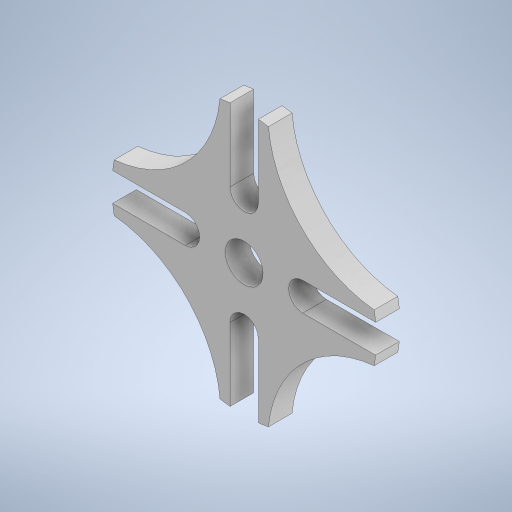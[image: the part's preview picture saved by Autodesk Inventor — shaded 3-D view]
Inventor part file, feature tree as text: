
AUTODESK INVENTOR PART (.ipt)
format: ipt  version: 2024 (Build 280153000, 153)  size: 276,480 bytes
history: native  units: mm
features: extrude x2, sketch x2, pattern_circular x1
ambient origin geometry x8: Origin, YZ Plane, XZ Plane, XY Plane, X Axis, Y Axis, Z Axis, Center Point
bodies: Solid1 (feature_tree)
feature tree (5):
  extrude  "Extrusion1"  Depth=5.0mm TaperAngle=0.0deg
  extrude  "Extrusion2"  Depth=5.0mm
  pattern_circular  "Circular Pattern1"  Count=6  [1 undecoded]
  sketch  "Sketch1"  dims[d0=56.0mm d1=5.0mm d2=0.0mm]
  sketch  "Sketch2"  dims[d3=30.0mm d4=30.0mm d5=60.0mm d6=60.0mm d7=50.0mm d8=8.0mm d9=6.0mm d10=5.0mm d11=0.0mm d12=40.0mm d13=360.0deg]
note: 1 required parameter value undecoded (feature->parameter linkage not recoverable at this tier; creation-order binding heuristic only, values carry confidence <= 0.55)
